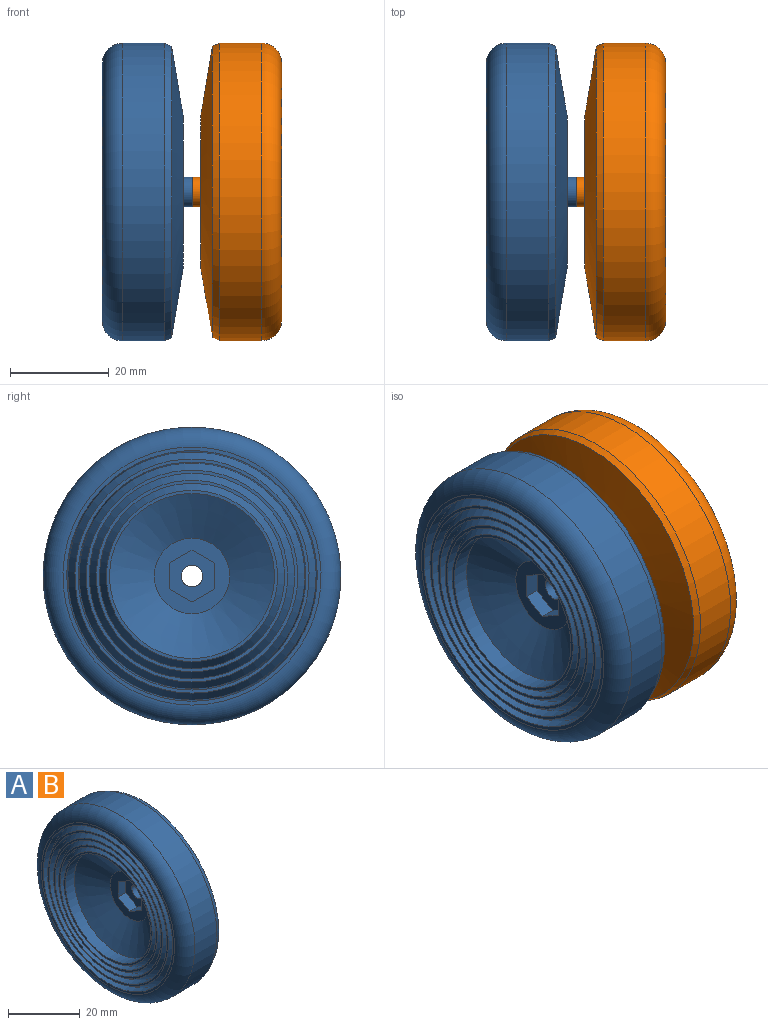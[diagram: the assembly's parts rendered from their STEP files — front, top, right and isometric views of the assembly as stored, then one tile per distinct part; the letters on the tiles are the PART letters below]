
ASSEMBLY  parts=2 mates=1
PART A: 39 faces, bbox 18.1x65.3x65.3 mm
  f0: cylinder r=2.2mm len=6.62mm, axis (1,0,0), area 91.4mm2, adj f29,f38
  f1: cylinder r=3.8mm len=7.6mm, axis (1,0,0), area 26.9mm2, adj f2,f31
  f2: plane 13.3x13.3mm, normal (1,0,0), area 93.6mm2, adj f1,f3
  f3: cylinder r=6.65mm len=13.3mm, axis (1,0,0), area 62.7mm2, adj f2,f4
  f4: plane 15.3x15.3mm, normal (1,0,0), area 44.9mm2, adj f3,f5
  f5: cylinder r=7.65mm len=15.3mm, axis (1,0,0), area 51.7mm2, adj f4,f6
  f6: plane 20.3x20.3mm, normal (1,0,0), area 139.8mm2, adj f5,f7
  f7: cylinder r=10.15mm len=20.3mm, axis (1,0,0), area 68.6mm2, adj f6,f8
  f8: plane 30.3x30.3mm, normal (1,0,0), area 397.4mm2, adj f7,f9
  f9: cone r=15.15mm half-angle=80.5deg, axis (-1,0,0), area 2045.1mm2, adj f8,f10
  f10: cone r=29.52mm half-angle=24.7deg, axis (-1,0,0), area 281.4mm2, adj f9,f11
  f11: cylinder r=30.15mm len=60.3mm, axis (1,0,0), area 1636mm2, adj f10,f12
  f12: torus R=26.15mm, axis (1,0,0), area 1132.9mm2, adj f11,f13
  f13: plane 52.3x52.3mm, normal (-1,0,0), area 124.1mm2, adj f12,f14
  f14: cone r=25.38mm half-angle=5.6deg, axis (-1,0,0), area 377.8mm2, adj f13,f15
  f15: cone r=23.72mm half-angle=31deg, axis (1,0,0), area 424.4mm2, adj f14,f16
  f16: plane 47.45x47.45mm, normal (-1,0,0), area 91.9mm2, adj f15,f17
  f17: cone r=23.1mm half-angle=5.6deg, axis (-1,0,0), area 343.7mm2, adj f16,f18
  f18: cone r=21.44mm half-angle=31deg, axis (1,0,0), area 384.8mm2, adj f17,f19
  f19: plane 42.88x42.88mm, normal (-1,0,0), area 83mm2, adj f18,f20
  f20: cylinder r=20.81mm len=41.63mm, axis (1,0,0), area 309.7mm2, adj f19,f21
  f21: cone r=19.39mm half-angle=31deg, axis (1,0,0), area 349.2mm2, adj f20,f22
  f22: plane 38.78x38.78mm, normal (-1,0,0), area 74.9mm2, adj f21,f23
  f23: cylinder r=18.76mm len=37.53mm, axis (1,0,0), area 279.2mm2, adj f22,f24
  f24: cone r=17.34mm half-angle=31deg, axis (1,0,0), area 313.5mm2, adj f23,f25
  f25: plane 34.68x34.68mm, normal (-1,0,0), area 66.9mm2, adj f24,f26
  f26: cylinder r=16.71mm len=33.43mm, axis (1,0,0), area 368mm2, adj f25,f27
  f27: cone r=16.71mm half-angle=61deg, axis (-1,0,0), area 793.5mm2, adj f26,f28
  f28: plane 15.28x15.28mm, normal (-1,0,0), area 111.8mm2, adj f27,f32,f33,f34,f35,f36,f37
  f29: plane 6x6mm, normal (1,0,0), area 13.1mm2, adj f0,f30
  f30: cylinder r=3mm len=6mm, axis (1,0,0), area 40.1mm2, adj f29,f31
  f31: plane 7.6x7.6mm, normal (1,0,0), area 17.1mm2, adj f1,f30
  f32: plane 5.25x3mm, normal (0,1,0), area 15.8mm2, adj f28,f33,f37,f38
  f33: plane 4.55x3mm, normal (0,0.5,-0.87), area 15.7mm2, adj f28,f32,f34,f38
  f34: plane 4.55x3mm, normal (0,-0.5,-0.87), area 15.7mm2, adj f28,f33,f35,f38
  f35: plane 5.25x3mm, normal (0,-1,0), area 15.8mm2, adj f28,f34,f36,f38
  f36: plane 4.55x3mm, normal (0,-0.5,0.87), area 15.7mm2, adj f28,f35,f37,f38
  f37: plane 4.55x3mm, normal (0,0.5,0.87), area 15.7mm2, adj f28,f32,f36,f38
  f38: plane 10.5x9.09mm, normal (-1,0,0), area 56.4mm2, adj f0,f32,f33,f34,f35,f36,f37
PART B: same geometry as A
PLACE A t=(-10.75,-0.73,-22.86)mm
PLACE B rot(axis=(0,1,0),180deg) t=(-9.25,-0.73,-22.86)mm
MATE fastened B.f0 <-> A.f0  axis (-1,0,0) through (-10,-0.73,-22.86)mm
